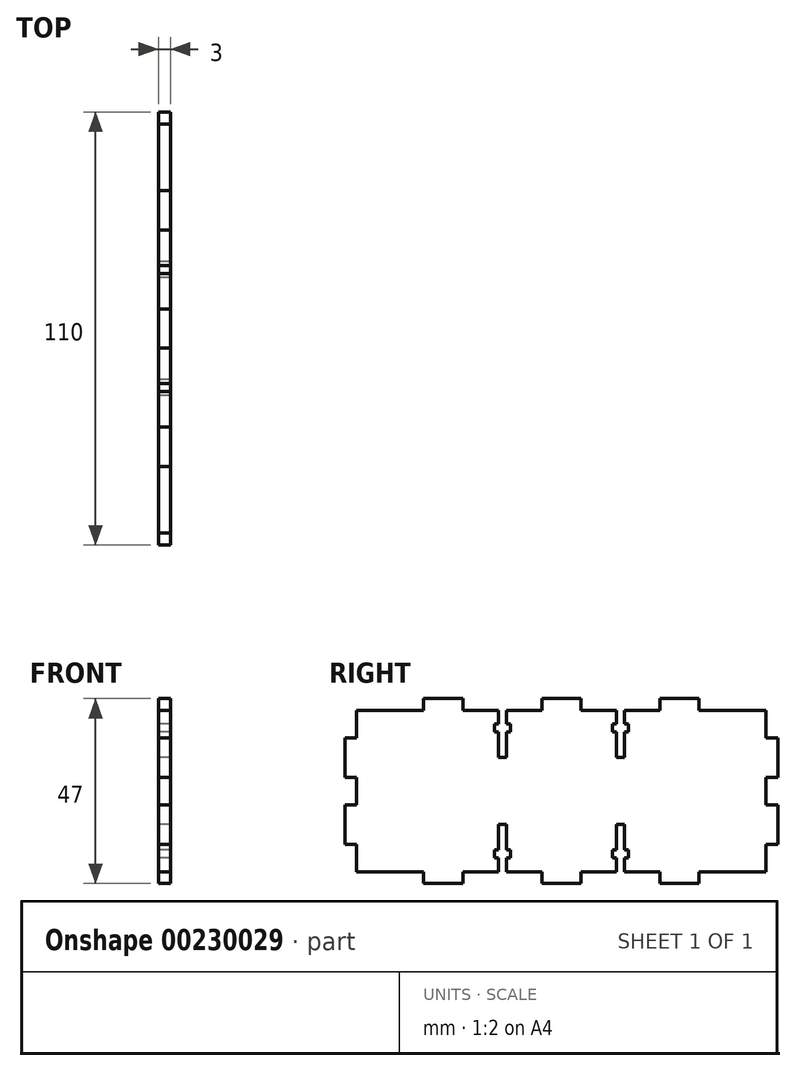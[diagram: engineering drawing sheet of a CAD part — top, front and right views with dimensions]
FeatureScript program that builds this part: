
annotation { "Feature Type Name" : "Feature", "Feature Type Description" : "" }
export const myFeature = defineFeature(function(context is Context, id is Id, definition is map)
    precondition{}
    {
        {
            var Q0;
            Q0=qCreatedBy(makeId("Right.planeOp"),FACE);
            var sketch = newSketch(context, id + "F0", { "sketchPlane" : qUnion([Q0])});
            skLineSegment(sketch, "E0", {"start": v(-52.38, -20.38) * mm, "end": v(-52.38, -13.38) * mm});
            skLineSegment(sketch, "E1", {"start": v(-52.38, -13.38) * mm, "end": v(-55.38, -13.38) * mm});
            skLineSegment(sketch, "E2", {"start": v(-55.38, -13.38) * mm, "end": v(-55.38, -3.38) * mm});
            skLineSegment(sketch, "E3", {"start": v(-55.38, -3.38) * mm, "end": v(-52.38, -3.38) * mm});
            skLineSegment(sketch, "E4", {"start": v(-52.38, -3.38) * mm, "end": v(-52.38, 0.12) * mm});
            skLineSegment(sketch, "E5", {"start": v(-52.38, -20.38) * mm, "end": v(-35.38, -20.38) * mm});
            skLineSegment(sketch, "E6", {"start": v(-35.38, -20.38) * mm, "end": v(-35.38, -23.38) * mm});
            skLineSegment(sketch, "E7", {"start": v(-35.38, -23.38) * mm, "end": v(-25.38, -23.38) * mm});
            skLineSegment(sketch, "E8", {"start": v(-25.38, -20.38) * mm, "end": v(-25.38, -23.38) * mm});
            skLineSegment(sketch, "E9", {"start": v(-25.38, -20.38) * mm, "end": v(-16.38, -20.38) * mm});
            skLineSegment(sketch, "E10", {"start": v(-16.38, -20.38) * mm, "end": v(-16.38, -16.88) * mm});
            skLineSegment(sketch, "E11", {"start": v(-16.38, -16.88) * mm, "end": v(-17.38, -16.88) * mm});
            skLineSegment(sketch, "E12", {"start": v(-17.38, -16.88) * mm, "end": v(-17.38, -14.88) * mm});
            skLineSegment(sketch, "E13", {"start": v(-17.38, -14.88) * mm, "end": v(-16.38, -14.88) * mm});
            skLineSegment(sketch, "E14", {"start": v(-16.38, -14.88) * mm, "end": v(-16.38, -8.38) * mm});
            skLineSegment(sketch, "E15", {"start": v(-16.38, -8.38) * mm, "end": v(-14.38, -8.38) * mm});
            skLineSegment(sketch, "E16", {"start": v(-14.38, -8.38) * mm, "end": v(-14.38, -14.88) * mm});
            skLineSegment(sketch, "E17", {"start": v(-14.38, -14.88) * mm, "end": v(-13.38, -14.88) * mm});
            skLineSegment(sketch, "E18", {"start": v(-14.38, -16.88) * mm, "end": v(-13.38, -16.88) * mm});
            skLineSegment(sketch, "E19", {"start": v(-14.38, -20.38) * mm, "end": v(-14.38, -16.88) * mm});
            skLineSegment(sketch, "E20", {"start": v(-14.38, -20.38) * mm, "end": v(-5.38, -20.38) * mm});
            skLineSegment(sketch, "E21", {"start": v(-13.38, -16.88) * mm, "end": v(-13.38, -14.88) * mm});
            skLineSegment(sketch, "E22", {"start": v(-5.38, -20.38) * mm, "end": v(-5.38, -23.38) * mm});
            skLineSegment(sketch, "E23", {"start": v(-5.38, -23.38) * mm, "end": v(-0.38, -23.38) * mm});
            skLineSegment(sketch, "E24", {"start": v(-52.38, 0.12) * mm, "end": v(-0.38, 0.12) * mm, "construction": true});
            skLineSegment(sketch, "E25", {"start": v(-0.38, 0.12) * mm, "end": v(-0.38, -23.38) * mm, "construction": true});
            skLineSegment(sketch, "E26.MirrorCS", {"start": v(-17.38, 15.12) * mm, "end": v(-16.38, 15.12) * mm});
            skLineSegment(sketch, "E27.MirrorCS", {"start": v(-13.38, 17.12) * mm, "end": v(-13.38, 15.12) * mm});
            skLineSegment(sketch, "E28.MirrorCS", {"start": v(-16.38, 17.12) * mm, "end": v(-17.38, 17.12) * mm});
            skLineSegment(sketch, "E29.MirrorCS", {"start": v(-17.38, 17.12) * mm, "end": v(-17.38, 15.12) * mm});
            skLineSegment(sketch, "E30.MirrorCS", {"start": v(-14.38, 15.12) * mm, "end": v(-13.38, 15.12) * mm});
            skLineSegment(sketch, "E31.MirrorCS", {"start": v(-14.38, 17.12) * mm, "end": v(-13.38, 17.12) * mm});
            skLineSegment(sketch, "E32.MirrorCS", {"start": v(-16.38, 8.62) * mm, "end": v(-14.38, 8.62) * mm});
            skLineSegment(sketch, "E33.MirrorCS", {"start": v(-16.38, 20.62) * mm, "end": v(-16.38, 17.12) * mm});
            skLineSegment(sketch, "E34.MirrorCS", {"start": v(-25.38, 20.62) * mm, "end": v(-25.38, 23.62) * mm});
            skLineSegment(sketch, "E35.MirrorCS", {"start": v(-52.38, 13.62) * mm, "end": v(-55.38, 13.62) * mm});
            skLineSegment(sketch, "E36.MirrorCS", {"start": v(-16.38, 15.12) * mm, "end": v(-16.38, 8.62) * mm});
            skLineSegment(sketch, "E37.MirrorCS", {"start": v(-14.38, 20.62) * mm, "end": v(-14.38, 17.12) * mm});
            skLineSegment(sketch, "E38.MirrorCS", {"start": v(-25.38, 20.62) * mm, "end": v(-16.38, 20.62) * mm});
            skLineSegment(sketch, "E39.MirrorCS", {"start": v(-14.38, 8.62) * mm, "end": v(-14.38, 15.12) * mm});
            skLineSegment(sketch, "E40.MirrorCS", {"start": v(-14.38, 20.62) * mm, "end": v(-5.38, 20.62) * mm});
            skLineSegment(sketch, "E41.MirrorCS", {"start": v(-52.38, 20.62) * mm, "end": v(-35.38, 20.62) * mm});
            skLineSegment(sketch, "E42.MirrorCS", {"start": v(-35.38, 20.62) * mm, "end": v(-35.38, 23.62) * mm});
            skLineSegment(sketch, "E43.MirrorCS", {"start": v(-55.38, 13.62) * mm, "end": v(-55.38, 3.62) * mm});
            skLineSegment(sketch, "E44.MirrorCS", {"start": v(-55.38, 3.62) * mm, "end": v(-52.38, 3.62) * mm});
            skLineSegment(sketch, "E45.MirrorCS", {"start": v(-52.38, 20.62) * mm, "end": v(-52.38, 13.62) * mm});
            skLineSegment(sketch, "E46.MirrorCS", {"start": v(-5.38, 20.62) * mm, "end": v(-5.38, 23.62) * mm});
            skLineSegment(sketch, "E47.MirrorCS", {"start": v(-35.38, 23.62) * mm, "end": v(-25.38, 23.62) * mm});
            skLineSegment(sketch, "E48.MirrorCS", {"start": v(-52.38, 3.62) * mm, "end": v(-52.38, 0.12) * mm});
            skLineSegment(sketch, "E49.MirrorCS", {"start": v(-5.38, 23.62) * mm, "end": v(-0.38, 23.62) * mm});
            skLineSegment(sketch, "E50.MirrorCS", {"start": v(-0.38, 0.12) * mm, "end": v(-0.38, 23.62) * mm, "construction": true});
            skLineSegment(sketch, "E51.MirrorCS", {"start": v(16.62, 17.12) * mm, "end": v(16.62, 15.12) * mm});
            skLineSegment(sketch, "E52.MirrorCS", {"start": v(16.62, 15.12) * mm, "end": v(15.62, 15.12) * mm});
            skLineSegment(sketch, "E53.MirrorCS", {"start": v(15.62, 8.62) * mm, "end": v(13.62, 8.62) * mm});
            skLineSegment(sketch, "E54.MirrorCS", {"start": v(13.62, 17.12) * mm, "end": v(12.62, 17.12) * mm});
            skLineSegment(sketch, "E55.MirrorCS", {"start": v(13.62, -16.88) * mm, "end": v(12.62, -16.88) * mm});
            skLineSegment(sketch, "E56.MirrorCS", {"start": v(15.62, -16.88) * mm, "end": v(16.62, -16.88) * mm});
            skLineSegment(sketch, "E57.MirrorCS", {"start": v(16.62, -16.88) * mm, "end": v(16.62, -14.88) * mm});
            skLineSegment(sketch, "E58.MirrorCS", {"start": v(13.62, -14.88) * mm, "end": v(12.62, -14.88) * mm});
            skLineSegment(sketch, "E59.MirrorCS", {"start": v(12.62, 17.12) * mm, "end": v(12.62, 15.12) * mm});
            skLineSegment(sketch, "E60.MirrorCS", {"start": v(13.62, 15.12) * mm, "end": v(12.62, 15.12) * mm});
            skLineSegment(sketch, "E61.MirrorCS", {"start": v(16.62, -14.88) * mm, "end": v(15.62, -14.88) * mm});
            skLineSegment(sketch, "E62.MirrorCS", {"start": v(12.62, -16.88) * mm, "end": v(12.62, -14.88) * mm});
            skLineSegment(sketch, "E63.MirrorCS", {"start": v(15.62, 17.12) * mm, "end": v(16.62, 17.12) * mm});
            skLineSegment(sketch, "E64.MirrorCS", {"start": v(15.62, -8.38) * mm, "end": v(13.62, -8.38) * mm});
            skLineSegment(sketch, "E65.MirrorCS", {"start": v(24.62, 20.62) * mm, "end": v(24.62, 23.62) * mm});
            skLineSegment(sketch, "E66.MirrorCS", {"start": v(13.62, -20.38) * mm, "end": v(4.62, -20.38) * mm});
            skLineSegment(sketch, "E67.MirrorCS", {"start": v(51.62, 20.62) * mm, "end": v(51.62, 13.62) * mm});
            skLineSegment(sketch, "E68.MirrorCS", {"start": v(34.62, 20.62) * mm, "end": v(34.62, 23.62) * mm});
            skLineSegment(sketch, "E69.MirrorCS", {"start": v(13.62, -20.38) * mm, "end": v(13.62, -16.88) * mm});
            skLineSegment(sketch, "E70.MirrorCS", {"start": v(13.62, -8.38) * mm, "end": v(13.62, -14.88) * mm});
            skLineSegment(sketch, "E71.MirrorCS", {"start": v(15.62, 15.12) * mm, "end": v(15.62, 8.62) * mm});
            skLineSegment(sketch, "E72.MirrorCS", {"start": v(51.62, 3.62) * mm, "end": v(51.62, 0.12) * mm});
            skLineSegment(sketch, "E73.MirrorCS", {"start": v(51.62, 13.62) * mm, "end": v(54.62, 13.62) * mm});
            skLineSegment(sketch, "E74.MirrorCS", {"start": v(34.62, 23.62) * mm, "end": v(24.62, 23.62) * mm});
            skLineSegment(sketch, "E75.MirrorCS", {"start": v(15.62, -20.38) * mm, "end": v(15.62, -16.88) * mm});
            skLineSegment(sketch, "E76.MirrorCS", {"start": v(15.62, 20.62) * mm, "end": v(15.62, 17.12) * mm});
            skLineSegment(sketch, "E77.MirrorCS", {"start": v(34.62, -20.38) * mm, "end": v(34.62, -23.38) * mm});
            skLineSegment(sketch, "E78.MirrorCS", {"start": v(51.62, -20.38) * mm, "end": v(51.62, -13.38) * mm});
            skLineSegment(sketch, "E79.MirrorCS", {"start": v(4.62, 23.62) * mm, "end": v(-0.38, 23.62) * mm});
            skLineSegment(sketch, "E80.MirrorCS", {"start": v(24.62, -20.38) * mm, "end": v(15.62, -20.38) * mm});
            skLineSegment(sketch, "E81.MirrorCS", {"start": v(4.62, -20.38) * mm, "end": v(4.62, -23.38) * mm});
            skLineSegment(sketch, "E82.MirrorCS", {"start": v(51.62, -13.38) * mm, "end": v(54.62, -13.38) * mm});
            skLineSegment(sketch, "E83.MirrorCS", {"start": v(24.62, 20.62) * mm, "end": v(15.62, 20.62) * mm});
            skLineSegment(sketch, "E84.MirrorCS", {"start": v(54.62, 13.62) * mm, "end": v(54.62, 3.62) * mm});
            skLineSegment(sketch, "E85.MirrorCS", {"start": v(54.62, -13.38) * mm, "end": v(54.62, -3.38) * mm});
            skLineSegment(sketch, "E86.MirrorCS", {"start": v(13.62, 8.62) * mm, "end": v(13.62, 15.12) * mm});
            skLineSegment(sketch, "E87.MirrorCS", {"start": v(4.62, -23.38) * mm, "end": v(-0.38, -23.38) * mm});
            skLineSegment(sketch, "E88.MirrorCS", {"start": v(13.62, 20.62) * mm, "end": v(13.62, 17.12) * mm});
            skLineSegment(sketch, "E89.MirrorCS", {"start": v(4.62, 20.62) * mm, "end": v(4.62, 23.62) * mm});
            skLineSegment(sketch, "E90.MirrorCS", {"start": v(13.62, 20.62) * mm, "end": v(4.62, 20.62) * mm});
            skLineSegment(sketch, "E91.MirrorCS", {"start": v(51.62, 0.12) * mm, "end": v(-0.38, 0.12) * mm, "construction": true});
            skLineSegment(sketch, "E92.MirrorCS", {"start": v(54.62, 3.62) * mm, "end": v(51.62, 3.62) * mm});
            skLineSegment(sketch, "E93.MirrorCS", {"start": v(51.62, -20.38) * mm, "end": v(34.62, -20.38) * mm});
            skLineSegment(sketch, "E94.MirrorCS", {"start": v(34.62, -23.38) * mm, "end": v(24.62, -23.38) * mm});
            skLineSegment(sketch, "E95.MirrorCS", {"start": v(15.62, -14.88) * mm, "end": v(15.62, -8.38) * mm});
            skLineSegment(sketch, "E96.MirrorCS", {"start": v(24.62, -20.38) * mm, "end": v(24.62, -23.38) * mm});
            skLineSegment(sketch, "E97.MirrorCS", {"start": v(51.62, 20.62) * mm, "end": v(34.62, 20.62) * mm});
            skLineSegment(sketch, "E98.MirrorCS", {"start": v(51.62, -3.38) * mm, "end": v(51.62, 0.12) * mm});
            skLineSegment(sketch, "E99.MirrorCS", {"start": v(54.62, -3.38) * mm, "end": v(51.62, -3.38) * mm});
            skSolve(sketch);
        }
        {
            var Q0;
            Q0 = qSketchRegion(id + "F0", true);
            extrude(context, id + "F1", {"entities" : qUnion([Q0]), "depth" : 3 * mm});
        }
    });
